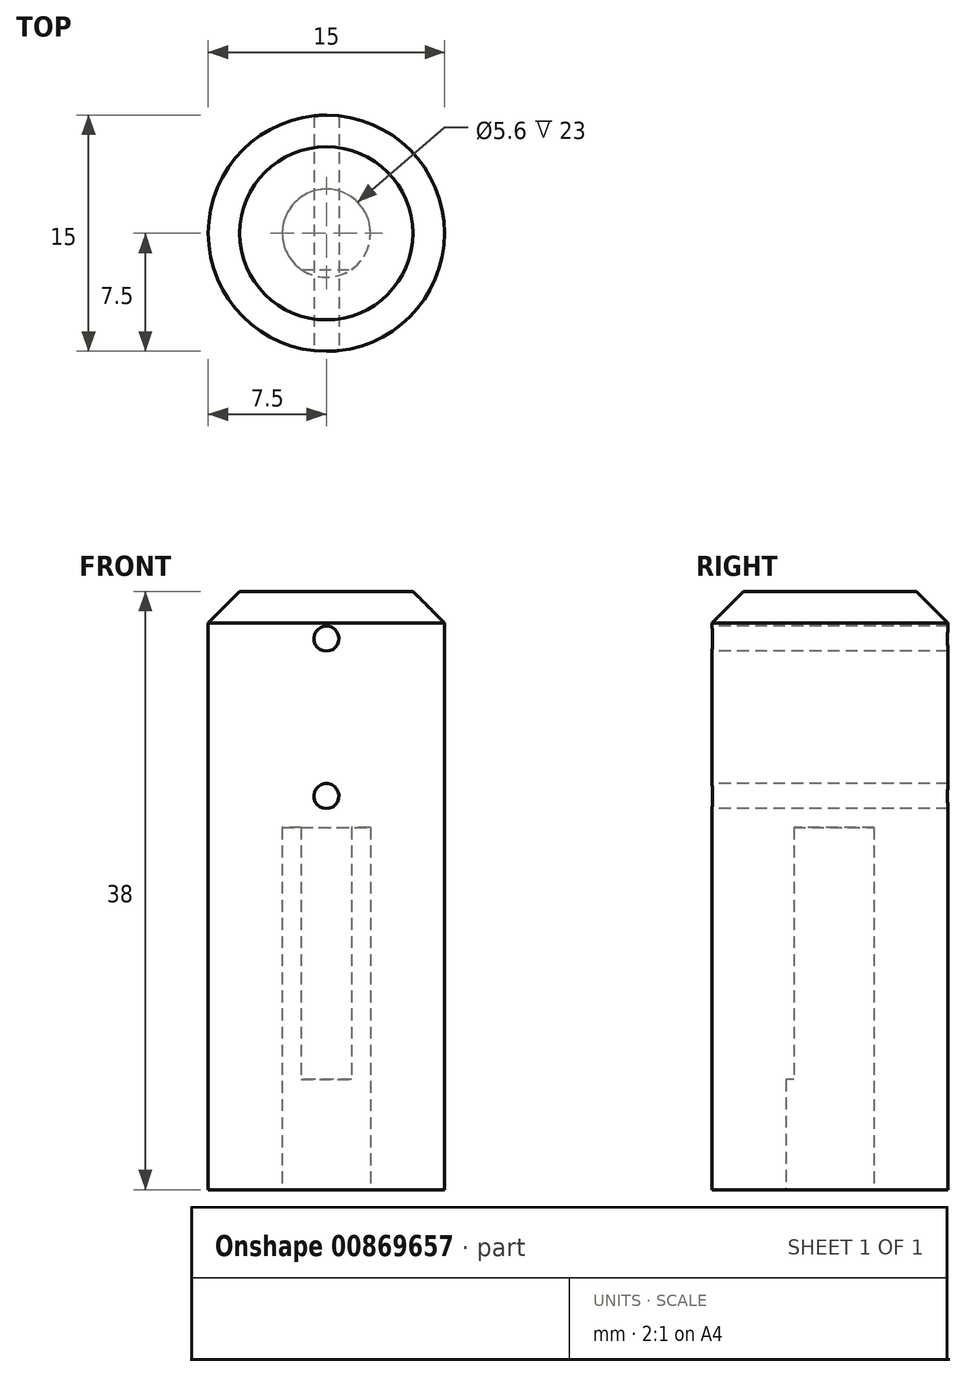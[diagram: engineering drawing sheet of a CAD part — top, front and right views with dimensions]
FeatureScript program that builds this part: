
annotation { "Feature Type Name" : "Feature", "Feature Type Description" : "" }
export const myFeature = defineFeature(function(context is Context, id is Id, definition is map)
    precondition{}
    {
        {
            var Q0;
            Q0=qCreatedBy(makeId("Top.planeOp"),FACE);
            var sketch = newSketch(context, id + "F0", { "sketchPlane" : qUnion([Q0])});
            skCircle(sketch, "E0", {"center": v(0, 0) * mm, "radius": 7.5 * mm});
            skSolve(sketch);
        }
        {
            var Q0;
            Q0=makeQuery(id+"F0.imprint","IMPRINT",FACE,{"disambiguationData":[TD([[makeQuery(id+"F0.imprint","IMPRINT",EDGE,{"derivedFrom":sQuery(id+"F0.wireOp",EDGE,"E0")}),1.0]])]});
            extrude(context, id + "F1", {"entities" : qUnion([Q0]), "depth" : 38 * mm, "offsetDistance" : 25 * mm});
        }
        {
            var Q0;
            Q0=qCreatedBy(makeId("Front.planeOp"),FACE);
            cPlane(context, id + "F2", {"entities" : qUnion([Q0]), "cplaneType" : CPlaneType.OFFSET, "offset" : 7.5 * mm, "width" : 150 * mm, "height" : 150 * mm});
        }
        {
            var Q0;
            Q0=qCreatedBy(id+"F2.planeOp",FACE);
            var sketch = newSketch(context, id + "F3", { "sketchPlane" : qUnion([Q0])});
            skCircle(sketch, "E1", {"center": v(0, 35) * mm, "radius": 0.8 * mm});
            skCircle(sketch, "E2", {"center": v(0, 25) * mm, "radius": 0.8 * mm});
            skSolve(sketch);
        }
        {
            var Q0;
            Q0=makeQuery(id+"F3.imprint","IMPRINT",FACE,{"disambiguationData":[TD([[makeQuery(id+"F3.imprint","IMPRINT",EDGE,{"derivedFrom":sQuery(id+"F3.wireOp",EDGE,"E1")}),1.0]])]});
            var Q1;
            Q1=makeQuery(id+"F3.imprint","IMPRINT",FACE,{"disambiguationData":[TD([[makeQuery(id+"F3.imprint","IMPRINT",EDGE,{"derivedFrom":sQuery(id+"F3.wireOp",EDGE,"E2")}),1.0]])]});
            extrude(context, id + "F4", {"entities" : qUnion([Q0, Q1]), "operationType" : NewBodyOperationType.REMOVE, "endBound" : BoundingType.THROUGH_ALL, "oppositeDirection" : true, "depth" : 25 * mm, "offsetDistance" : 25 * mm});
        }
        {
            var Q0;
            Q0=makeQuery(id+"F1.opExtrude","CAP_EDGE",EDGE,{"disambiguationData":[OSD([sQuery(id+"F0.wireOp",EDGE,"E0")])],"isStart":false});
            chamfer(context, id + "F5", {"entities" : qUnion([Q0]), "width" : 2 * mm, "tangentPropagation" : true});
        }
        {
            var Q0;
            Q0=makeQuery(id+"F1.opExtrude","CAP_FACE",FACE,{"disambiguationData":[OSD([sQuery(id+"F0.wireOp",EDGE,"E0")])],"isStart":true});
            var sketch = newSketch(context, id + "F6", { "sketchPlane" : qUnion([Q0])});
            skCircle(sketch, "E3", {"center": v(0, 0) * mm, "radius": 2.8 * mm});
            skLineSegment(sketch, "E4", {"start": v(-1.6, 2.3) * mm, "end": v(1.6, 2.3) * mm});
            skSolve(sketch);
        }
        {
            var Q0;
            {var subQ0=sQuery(id+"F6.wireOp",EDGE,"E4");Q0=makeQuery(id+"F6.imprint","IMPRINT",FACE,{"disambiguationData":[TD([[makeQuery(id+"F6.imprint","IMPRINT",EDGE,{"derivedFrom":subQ0}),-1.0]])]});}
            extrude(context, id + "F7", {"entities" : qUnion([Q0]), "operationType" : NewBodyOperationType.REMOVE, "oppositeDirection" : true, "depth" : 23 * mm, "offsetDistance" : 25 * mm});
        }
        {
            var Q0;
            {var subQ0=sQuery(id+"F6.wireOp",EDGE,"E4");Q0=makeQuery(id+"F6.imprint","IMPRINT",FACE,{"disambiguationData":[TD([[makeQuery(id+"F6.imprint","IMPRINT",EDGE,{"derivedFrom":subQ0}),1.0]])]});}
            extrude(context, id + "F8", {"entities" : qUnion([Q0]), "operationType" : NewBodyOperationType.REMOVE, "oppositeDirection" : true, "depth" : 7 * mm, "offsetDistance" : 25 * mm});
        }
    });
